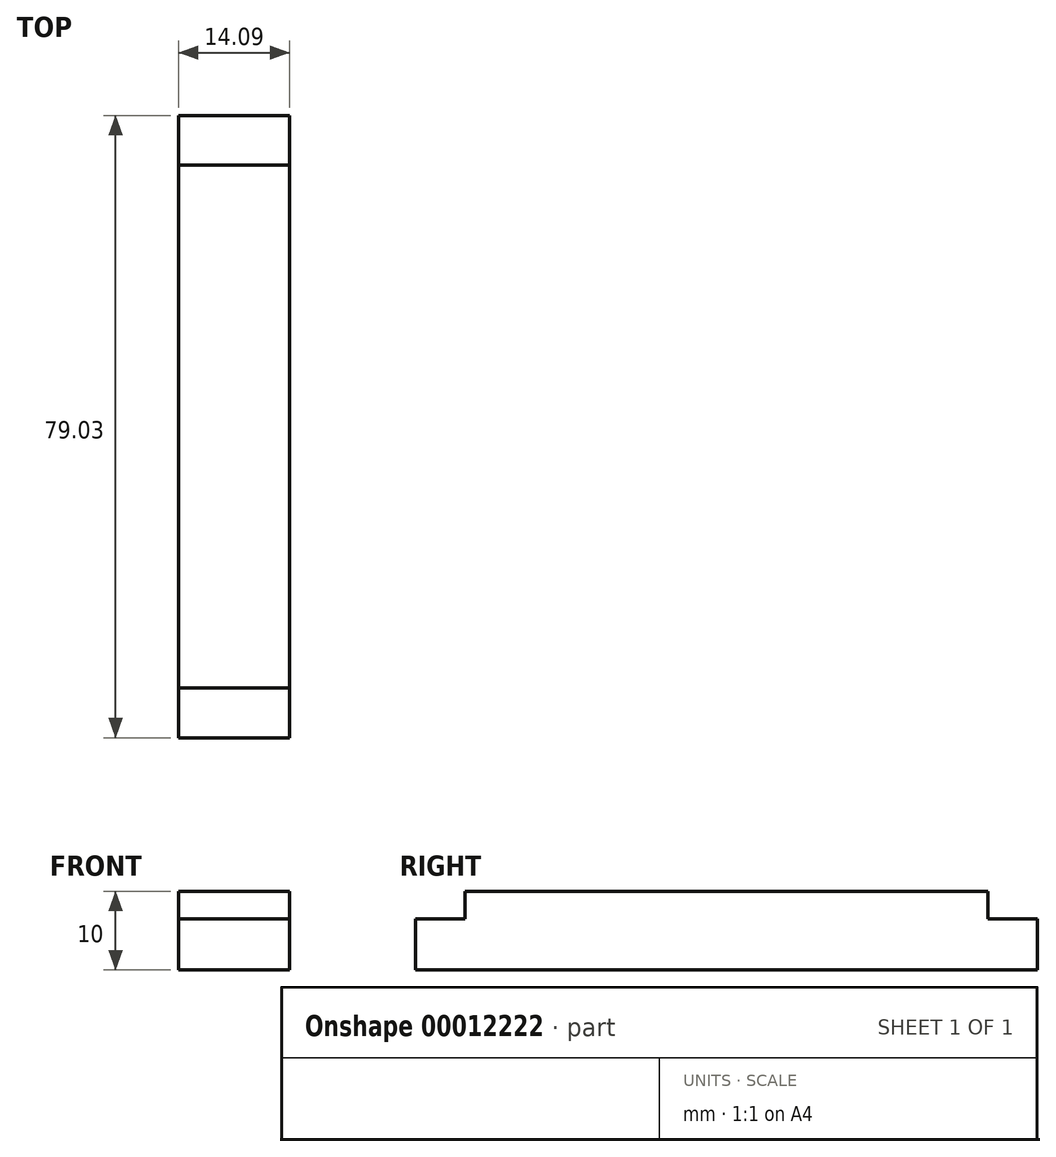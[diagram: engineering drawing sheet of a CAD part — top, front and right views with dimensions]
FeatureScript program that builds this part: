
annotation { "Feature Type Name" : "Feature", "Feature Type Description" : "" }
export const myFeature = defineFeature(function(context is Context, id is Id, definition is map)
    precondition{}
    {
        {
            var Q0;
            Q0=qCreatedBy(makeId("Top.planeOp"),FACE);
            var sketch = newSketch(context, id + "F0", { "sketchPlane" : qUnion([Q0])});
            skText(sketch, "E0", { "text": "I", "fontName": "OpenSans-Bold.ttf"});
            const initialGuessF0  = {"E0": [-0.02245, 0, 1, 0, 0.067]};
            skSetInitialGuess(sketch, initialGuessF0);
            skSolve(sketch);
        }
        {
            var Q0;
            Q0=makeQuery(id+"F0.imprint","IMPRINT",FACE,{"disambiguationData":[TD([[makeQuery(id+"F0.imprint","IMPRINT",EDGE,{"derivedFrom":sQuery(id+"F0.wireOp",EDGE,"E0.sketch_text.stroke-0")}),-1.0]])]});
            extrude(context, id + "F1", {"entities" : qUnion([Q0]), "depth" : 10 * mm});
        }
        {
            var Q0;
            Q0=makeQuery(id+"F1.opExtrude","SWEPT_FACE",FACE,{"disambiguationData":[OSD([sQuery(id+"F0.wireOp",EDGE,"E0.sketch_text.stroke-3")])]});
            var sketch = newSketch(context, id + "F2", { "sketchPlane" : qUnion([Q0])});
            skLineSegment(sketch, "E1.0.0", {"start": v(-14.09, 0) * mm, "end": v(0, 0) * mm});
            skLineSegment(sketch, "E1.0.1", {"start": v(0, 0) * mm, "end": v(0, 10) * mm});
            skLineSegment(sketch, "E1.0.2", {"start": v(0, 10) * mm, "end": v(-14.09, 10) * mm});
            skLineSegment(sketch, "E1.0.3", {"start": v(-14.09, 10) * mm, "end": v(-14.09, 0) * mm});
            skLineSegment(sketch, "E2.top", {"start": v(-14.09, 6.5) * mm, "end": v(0, 6.5) * mm});
            skLineSegment(sketch, "E2.left", {"start": v(-14.09, 0) * mm, "end": v(-14.09, 6.5) * mm});
            skLineSegment(sketch, "E2.right", {"start": v(0, 0) * mm, "end": v(0, 6.5) * mm});
            skSolve(sketch);
        }
        {
            var Q0;
            Q0=makeQuery(id+"F2.imprint","IMPRINT",FACE,{"disambiguationData":[TD([[makeQuery(id+"F2.imprint","IMPRINT",EDGE,{"derivedFrom":sQuery(id+"F2.wireOp",EDGE,"E1.0.0")}),-1.0]])]});
            extrude(context, id + "F3", {"entities" : qUnion([Q0]), "operationType" : NewBodyOperationType.ADD, "depth" : 6.3 * mm});
        }
        {
            var Q0;
            Q0=makeQuery(id+"F1.opExtrude","SWEPT_FACE",FACE,{"disambiguationData":[OSD([sQuery(id+"F0.wireOp",EDGE,"E0.sketch_text.stroke-1")])]});
            var sketch = newSketch(context, id + "F4", { "sketchPlane" : qUnion([Q0])});
            skLineSegment(sketch, "E3.0.0", {"start": v(0, 0) * mm, "end": v(14.09, 0) * mm});
            skLineSegment(sketch, "E3.0.1", {"start": v(14.09, 0) * mm, "end": v(14.09, 10) * mm});
            skLineSegment(sketch, "E3.0.2", {"start": v(14.09, 10) * mm, "end": v(0, 10) * mm});
            skLineSegment(sketch, "E3.0.3", {"start": v(0, 10) * mm, "end": v(0, 0) * mm});
            skLineSegment(sketch, "E4.top", {"start": v(0, 6.5) * mm, "end": v(14.09, 6.5) * mm});
            skLineSegment(sketch, "E4.left", {"start": v(0, 0) * mm, "end": v(0, 6.5) * mm});
            skLineSegment(sketch, "E4.right", {"start": v(14.09, 0) * mm, "end": v(14.09, 6.5) * mm});
            skSolve(sketch);
        }
        {
            var Q0;
            Q0=makeQuery(id+"F4.imprint","IMPRINT",FACE,{"disambiguationData":[TD([[makeQuery(id+"F4.imprint","IMPRINT",EDGE,{"derivedFrom":sQuery(id+"F4.wireOp",EDGE,"E3.0.0")}),-1.0]])]});
            extrude(context, id + "F5", {"entities" : qUnion([Q0]), "operationType" : NewBodyOperationType.ADD, "depth" : 6.3 * mm});
        }
    });
